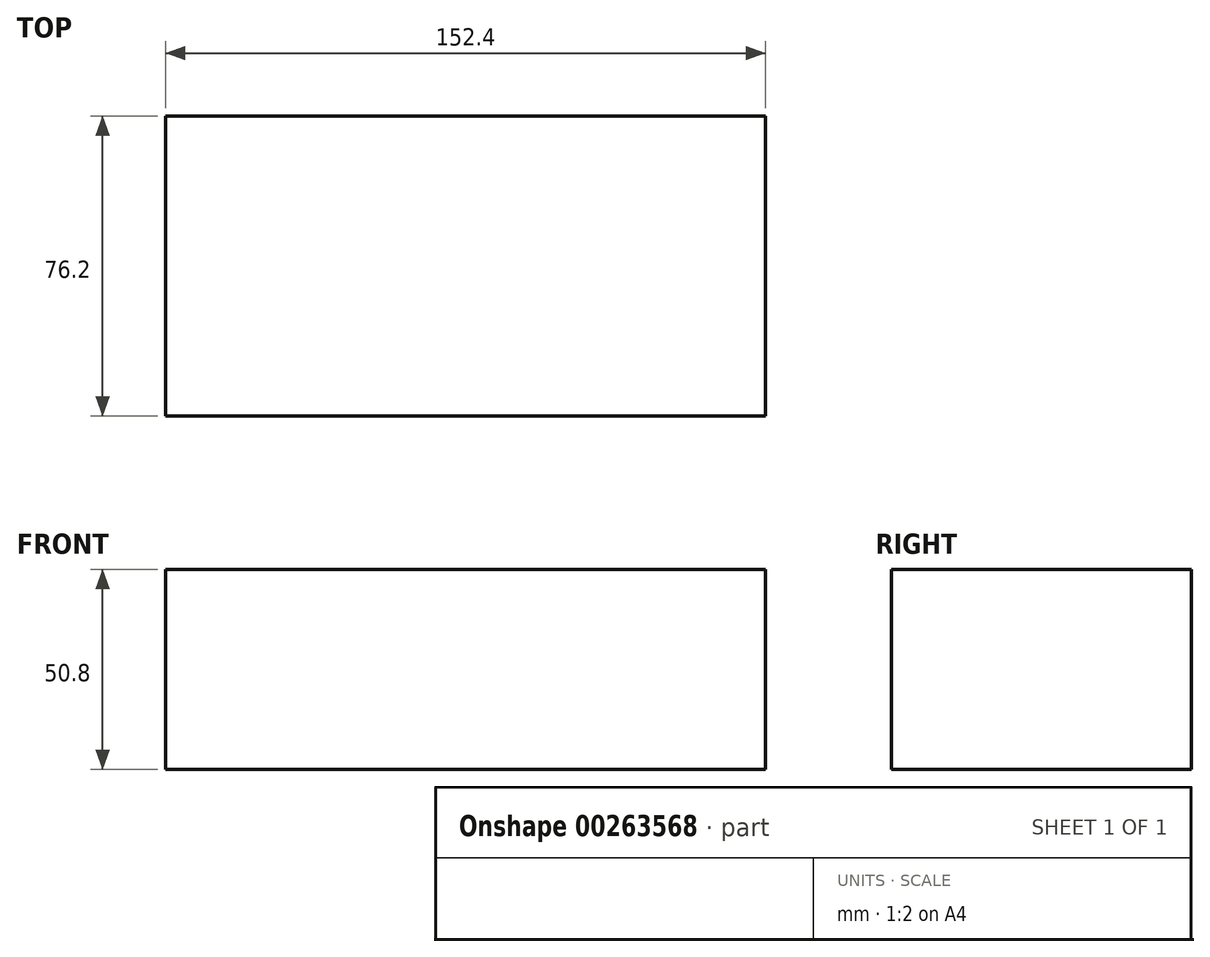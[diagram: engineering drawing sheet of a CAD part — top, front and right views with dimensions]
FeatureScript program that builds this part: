
annotation { "Feature Type Name" : "Feature", "Feature Type Description" : "" }
export const myFeature = defineFeature(function(context is Context, id is Id, definition is map)
    precondition{}
    {
        {
            var Q0;
            Q0=qCreatedBy(makeId("Front.planeOp"),FACE);
            var sketch = newSketch(context, id + "F0", { "sketchPlane" : qUnion([Q0])});
            skLineSegment(sketch, "E0", {"start": v(-47.2, -27.63) * mm, "end": v(105.2, -27.63) * mm});
            skLineSegment(sketch, "E1", {"start": v(-47.2, -27.63) * mm, "end": v(-47.2, 23.17) * mm});
            skLineSegment(sketch, "E2", {"start": v(-47.2, 23.17) * mm, "end": v(105.2, 23.17) * mm});
            skLineSegment(sketch, "E3", {"start": v(105.2, 23.17) * mm, "end": v(105.2, -27.63) * mm});
            skSolve(sketch);
        }
        {
            var Q0;
            Q0=makeQuery(id+"F0.imprint","IMPRINT",FACE,{"disambiguationData":[TD([[makeQuery(id+"F0.imprint","IMPRINT",EDGE,{"derivedFrom":sQuery(id+"F0.wireOp",EDGE,"E0")}),1.0]])]});
            extrude(context, id + "F1", {"entities" : qUnion([Q0]), "depth" : 76.2 * mm});
        }
    });
